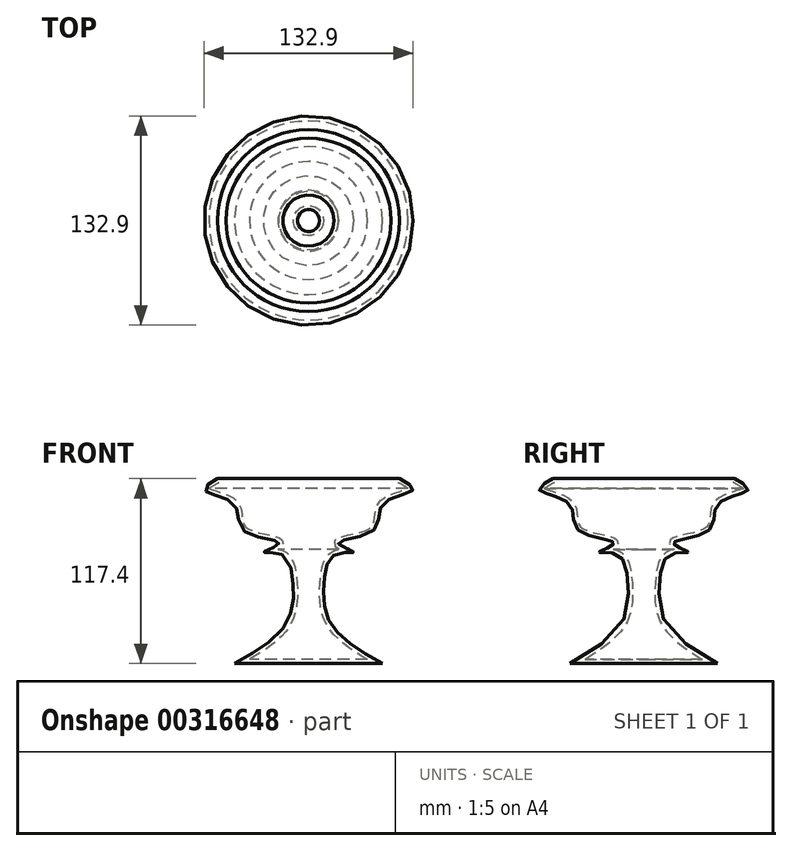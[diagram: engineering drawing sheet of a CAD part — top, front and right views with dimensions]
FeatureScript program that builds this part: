
annotation { "Feature Type Name" : "Feature", "Feature Type Description" : "" }
export const myFeature = defineFeature(function(context is Context, id is Id, definition is map)
    precondition{}
    {
        {
            var Q0;
            Q0=qCreatedBy(makeId("Front.planeOp"),FACE);
            var sketch = newSketch(context, id + "F0", { "sketchPlane" : qUnion([Q0])});
            skLineSegment(sketch, "E0", {"start": v(0, 75.95) * mm, "end": v(0, -50.27) * mm, "construction": true});
            skLineSegment(sketch, "E1", {"start": v(0, -50.27) * mm, "end": v(-46.98, -50.27) * mm});
            skFitSpline(sketch, "E2", {"points": [v(-46.98, -50.27) * mm, v(-13.9, -24.64) * mm, v(-10.05, 3.2) * mm, v(-17.5, 19.18) * mm, v(-28.51, 20.56) * mm, v(-18.87, 26.07) * mm, v(-41.47, 34.34) * mm, v(-46.98, 50.87) * mm, v(-66.27, 59.97) * mm, v(-57.73, 67.13) * mm], "startDerivative": vector(249.17, 140.99) * mm, "endDerivative": vector(173.67, 93.3) * mm});
            skLineSegment(sketch, "E3", {"start": v(-57.73, 67.13) * mm, "end": v(0, 67.13) * mm});
            skLineSegment(sketch, "E4", {"start": v(0, 67.13) * mm, "end": v(0, -50.27) * mm});
            skSolve(sketch);
        }
        {
            var Q0;
            Q0=makeQuery(id+"F0.imprint","IMPRINT",FACE,{"disambiguationData":[TD([[makeQuery(id+"F0.imprint","IMPRINT",EDGE,{"derivedFrom":sQuery(id+"F0.wireOp",EDGE,"E1")}),-1.0]])]});
            var Q1;
            Q1=sQuery(id+"F0.wireOp",EDGE,"E4");
            revolve(context, id + "F1", {"entities" : qUnion([Q0]), "axis" : qUnion([Q1]), "revolveType" : RevolveType.FULL});
        }
        {
            var Q0;
            Q0=makeQuery(id+"F1.opRevolve","SWEPT_FACE",FACE,{"disambiguationData":[OSD([sQuery(id+"F0.wireOp",EDGE,"E3")])]});
            shell(context, id + "F2", {"entities" : qUnion([Q0]), "thickness" : 2.54 * mm});
        }
    });
